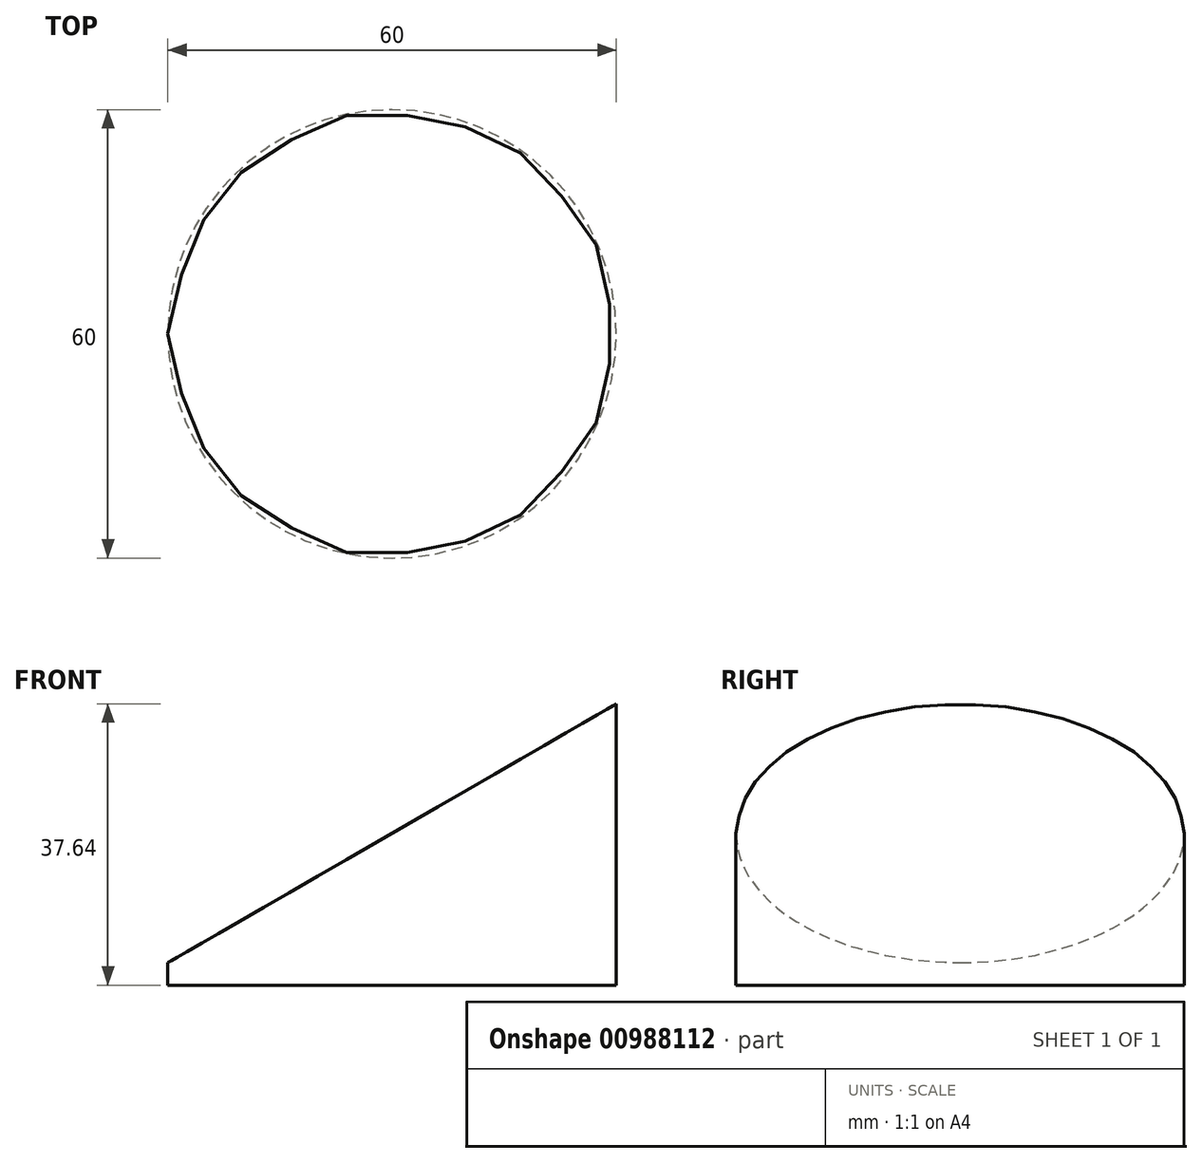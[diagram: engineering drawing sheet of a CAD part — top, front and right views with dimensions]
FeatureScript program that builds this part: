
annotation { "Feature Type Name" : "Feature", "Feature Type Description" : "" }
export const myFeature = defineFeature(function(context is Context, id is Id, definition is map)
    precondition{}
    {
        {
            var Q0;
            Q0=qCreatedBy(makeId("Top.planeOp"),FACE);
            var sketch = newSketch(context, id + "F0", { "sketchPlane" : qUnion([Q0])});
            skCircle(sketch, "E0", {"center": v(0, 0) * mm, "radius": 30 * mm});
            skSolve(sketch);
        }
        {
            var Q0;
            Q0 = qSketchRegion(id + "F0", true);
            extrude(context, id + "F1", {"entities" : qUnion([Q0]), "depth" : 40 * mm, "offsetDistance" : 25 * mm});
        }
        {
            var Q0;
            Q0=qCreatedBy(makeId("Front.planeOp"),FACE);
            var sketch = newSketch(context, id + "F2", { "sketchPlane" : qUnion([Q0])});
            skLineSegment(sketch, "E1", {"start": v(-41.2, 3) * mm, "end": v(37.21, 3) * mm, "construction": true});
            skLineSegment(sketch, "E2", {"start": v(-30, 0) * mm, "end": v(-30, 25) * mm, "construction": true});
            skLineSegment(sketch, "E3", {"start": v(-30, 3) * mm, "end": v(30, 37.64) * mm});
            skLineSegment(sketch, "E4", {"start": v(-30, 3) * mm, "end": v(-35.12, 3) * mm});
            skLineSegment(sketch, "E5", {"start": v(-35.12, 3) * mm, "end": v(-35.12, 50.68) * mm});
            skLineSegment(sketch, "E6", {"start": v(-35.12, 50.68) * mm, "end": v(35.45, 50.68) * mm});
            skLineSegment(sketch, "E7", {"start": v(35.45, 50.68) * mm, "end": v(35.45, 37.64) * mm});
            skLineSegment(sketch, "E8", {"start": v(35.45, 37.64) * mm, "end": v(30, 37.64) * mm});
            skSolve(sketch);
        }
        {
            var Q0;
            Q0 = qSketchRegion(id + "F2", true);
            extrude(context, id + "F3", {"entities" : qUnion([Q0]), "operationType" : NewBodyOperationType.REMOVE, "endBound" : BoundingType.THROUGH_ALL, "oppositeDirection" : true, "depth" : 25 * mm, "offsetDistance" : 25 * mm, "hasSecondDirection" : true, "secondDirectionBound" : SecondDirectionBoundingType.THROUGH_ALL, "secondDirectionOppositeDirection" : false, "secondDirectionDepth" : 25 * mm});
        }
    });
